# Revit family: SIVACON 8MF__
name_source: partatom
category: Electrical Fixtures
revit_build: Autodesk Revit 2016 (Build: 20160314_0715(x64)
units: mm (PartAtom-declared; Revit-internal decimal feet)

## family parameters
Always vertical = Yes
Cut with Voids When Loaded = No
Maintain Annotation Orientation = No
OmniClass Number = 23.80.00.00
OmniClass Title = Electric Power and Lighting
Part Type = Normal
Room Calculation Point = No
Round Connector Dimension = Use Diameter
Shared = No
Work Plane-Based = No

## types (4) — shared parameters
Base height = 0; 100mm; 200mm
Cable entry = bottom
Connection to plant = bottom
Connection type = Cable
Consultant support for Totally Integrated Power (TIP) = www.siemens.com/tip-cs
D_1 = D : 0400
D_2 = D : 0500
D_3 = D : 0600
D_4 = D : 0800
D_5 = D : 1200
Degree of protection = IP20; IP40; IP55
Electromagnetic compatibility (EMC) = without; with
Function = Control
H_1 = H : H 1800 Socket None
H_2 = H : H 1800 Socket 100
H_3 = H : H 1800 Socket 200
H_4 = H : H 2000 Socket None
H_5 = H : H 2000 Socket 100
H_6 = H : H 2000 Socket 200
H_7 = H : H 2200 Socket None
H_8 = H : H 2200 Socket 100
H_9 = H : H 2200 Socket 200
IFC Classification = Electric Distribution
Manufacturer = Siemens AG
Material main = Sheet steel (thickeness: 1.5mm;  frame 2,5mm)
Order number = 8MF...
Panel coating = Sendzimir-galvanised and powder-coated
Panel type = Empty panel
Panneling color = RAL7035; design parts: Petrol
Plant depth = 400mm; 500mm; 600mm; 800mm; 1000mm
Product Guid = 28c81f15-efba-4c2d-9222-3132d3c14dbe
Product data url = https://bimobject.com
SIMARIS planning tools = www.siemens.com/simaris
Seismic safety = without; with
Specification texts = www.siemens.com/specifications
Standards = IEC
Switchboard type = SIVACON 8MF
Technical description LV-switchboard = www.siemens.com
Type of arrangement = wall-standing; free-standing; extendable
W_1 = W : 0600
W_2 = W : 0800
W_3 = W : 0900
W_4 = W : 1000
W_5 = W : 1200
zero-valued in all types: Edition number

## per-type parameters (varying)
| type | EMC | IP_Typ | Model | Natural ventilation |
| SIVACON 8MF IP20 natural ventilation | without | 20 | Cubicle IP20 natural ventilation | with |
| SIVACON 8MF IP40 | without | 40 | Cubicle IP40 | without |
| SIVACON 8MF IP40 EMC | with | 401 | Cubicle IP40 EMC | without |
| SIVACON 8MF IP55 (Door plain) | without | 55 | Cubicle IP55 (Door plain) | without |

## geometry (parser evidence)
native form markers: Blend x9
no freeform markers — native parametric forms only
